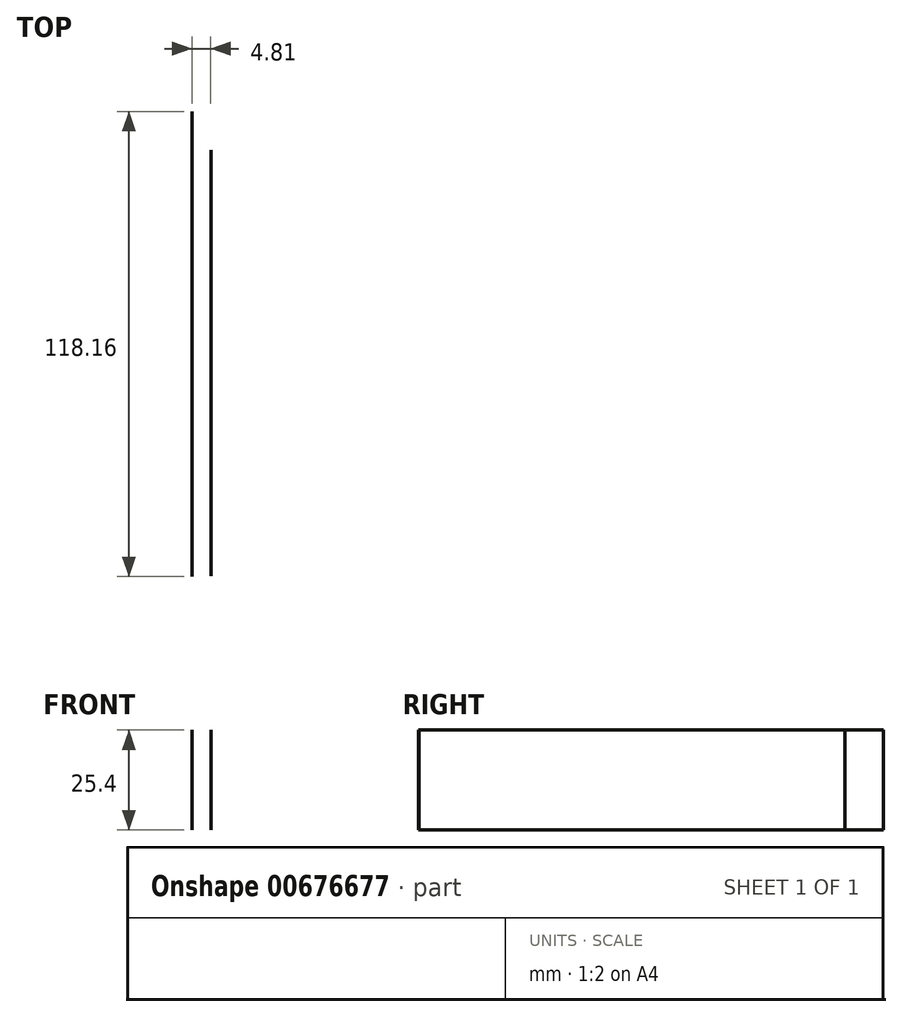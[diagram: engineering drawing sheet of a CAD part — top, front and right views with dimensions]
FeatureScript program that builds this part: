
annotation { "Feature Type Name" : "Feature", "Feature Type Description" : "" }
export const myFeature = defineFeature(function(context is Context, id is Id, definition is map)
    precondition{}
    {
        {
            var Q0;
            Q0=qCreatedBy(makeId("Top.planeOp"),FACE);
            var sketch = newSketch(context, id + "F0", { "sketchPlane" : qUnion([Q0])});
            skLineSegment(sketch, "E0", {"start": v(-59.27, 59.38) * mm, "end": v(-59.27, -58.78) * mm});
            skLineSegment(sketch, "E1", {"start": v(-59.27, -58.78) * mm, "end": v(-59.27, 59.38) * mm});
            skLineSegment(sketch, "E2", {"start": v(-56.3, 60.33) * mm, "end": v(-59.12, 59.1) * mm});
            skLineSegment(sketch, "E3", {"start": v(-59.12, 59.1) * mm, "end": v(57.7, 59.99) * mm});
            skLineSegment(sketch, "E4", {"start": v(57.7, 59.99) * mm, "end": v(57.7, -59.53) * mm});
            skLineSegment(sketch, "E5", {"start": v(57.7, -59.53) * mm, "end": v(49.8, -59.53) * mm});
            skLineSegment(sketch, "E6", {"start": v(49.8, -59.53) * mm, "end": v(49.8, 52.7) * mm});
            skLineSegment(sketch, "E7", {"start": v(-53.84, 52.63) * mm, "end": v(49.8, 52.7) * mm});
            skLineSegment(sketch, "E8", {"start": v(-54.46, 49.59) * mm, "end": v(-54.46, -58.68) * mm});
            skLineSegment(sketch, "E9", {"start": v(-54.46, -58.68) * mm, "end": v(-53.84, 52.63) * mm});
            skLineSegment(sketch, "E10", {"start": v(-50.01, -58.68) * mm, "end": v(-59.27, -58.78) * mm});
            skSolve(sketch);
        }
        {
            var Q0;
            Q0=sQuery(id+"F0.wireOp",EDGE,"E8");
            var Q1;
            Q1=sQuery(id+"F0.wireOp",EDGE,"E1");
            extrude(context, id + "F1", {"bodyType" : ToolBodyType.SURFACE, "operationType" : NewBodyOperationType.ADD, "surfaceEntities" : qUnion([Q0, Q1]), "depth" : 25.4 * mm, "offsetDistance" : 25.4 * mm});
        }
    });
